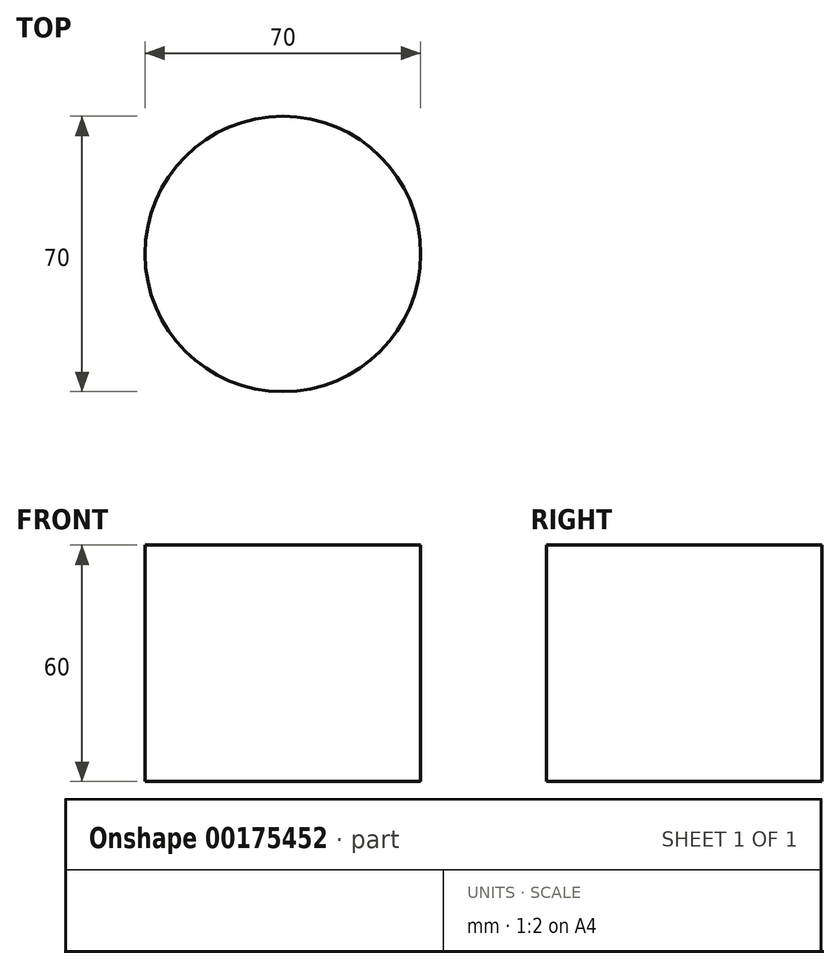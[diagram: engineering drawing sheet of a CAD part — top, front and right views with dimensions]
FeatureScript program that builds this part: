
annotation { "Feature Type Name" : "Feature", "Feature Type Description" : "" }
export const myFeature = defineFeature(function(context is Context, id is Id, definition is map)
    precondition{}
    {
        {
            var Q0;
            Q0=qCreatedBy(makeId("Top.planeOp"),FACE);
            var sketch = newSketch(context, id + "F0", { "sketchPlane" : qUnion([Q0])});
            skCircle(sketch, "E0", {"center": v(-23.7, 21.25) * mm, "radius": 35 * mm});
            skSolve(sketch);
        }
        {
            var Q0;
            Q0=sQuery(id+"F0.wireOp",EDGE,"E0");
            extrude(context, id + "F1", {"bodyType" : ToolBodyType.SURFACE, "surfaceEntities" : qUnion([Q0]), "depth" : 60 * mm});
        }
    });
